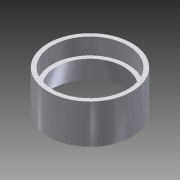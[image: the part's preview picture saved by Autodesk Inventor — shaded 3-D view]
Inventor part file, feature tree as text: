
AUTODESK INVENTOR PART (.ipt)
format: ipt  version: 2015 (Build 190159000, 159)  size: 133,632 bytes
history: native  units: in
note: dims shown in document units (in); Inventor stores cm internally (conversion verified against a paired STEP export)
features: revolve x1, sketch x1
ambient origin geometry x8: Origin, YZ Plane, XZ Plane, XY Plane, X Axis, Y Axis, Z Axis, Center Point
bodies: Solid1 (feature_tree)
feature tree (2):
  revolve  "Revolution1"  [1 undecoded]
  sketch  "Sketch1"  dims[d0=0.75in d1=1.0in d2=0.2185in d3=2.594in d4=0.5841in d5=0.5in d6=1.844in d7=0.5in d8=1.75in d9=0.25in d10=105.0deg d11=0.5in d12=0.5in d13=0.25in d14=0.375in d15=2.0in d16=0.5in d17=0.25in d18=0.234in d19=0.25in d20=2.0in d21=0.25in d22=105.0deg d23=0.125in d24=0.25in d25=2.3995in d26=0.125in d27=0.25in d28=180.0deg]
note: 1 required parameter value undecoded (feature->parameter linkage not recoverable at this tier; creation-order binding heuristic only, values carry confidence <= 0.55)
